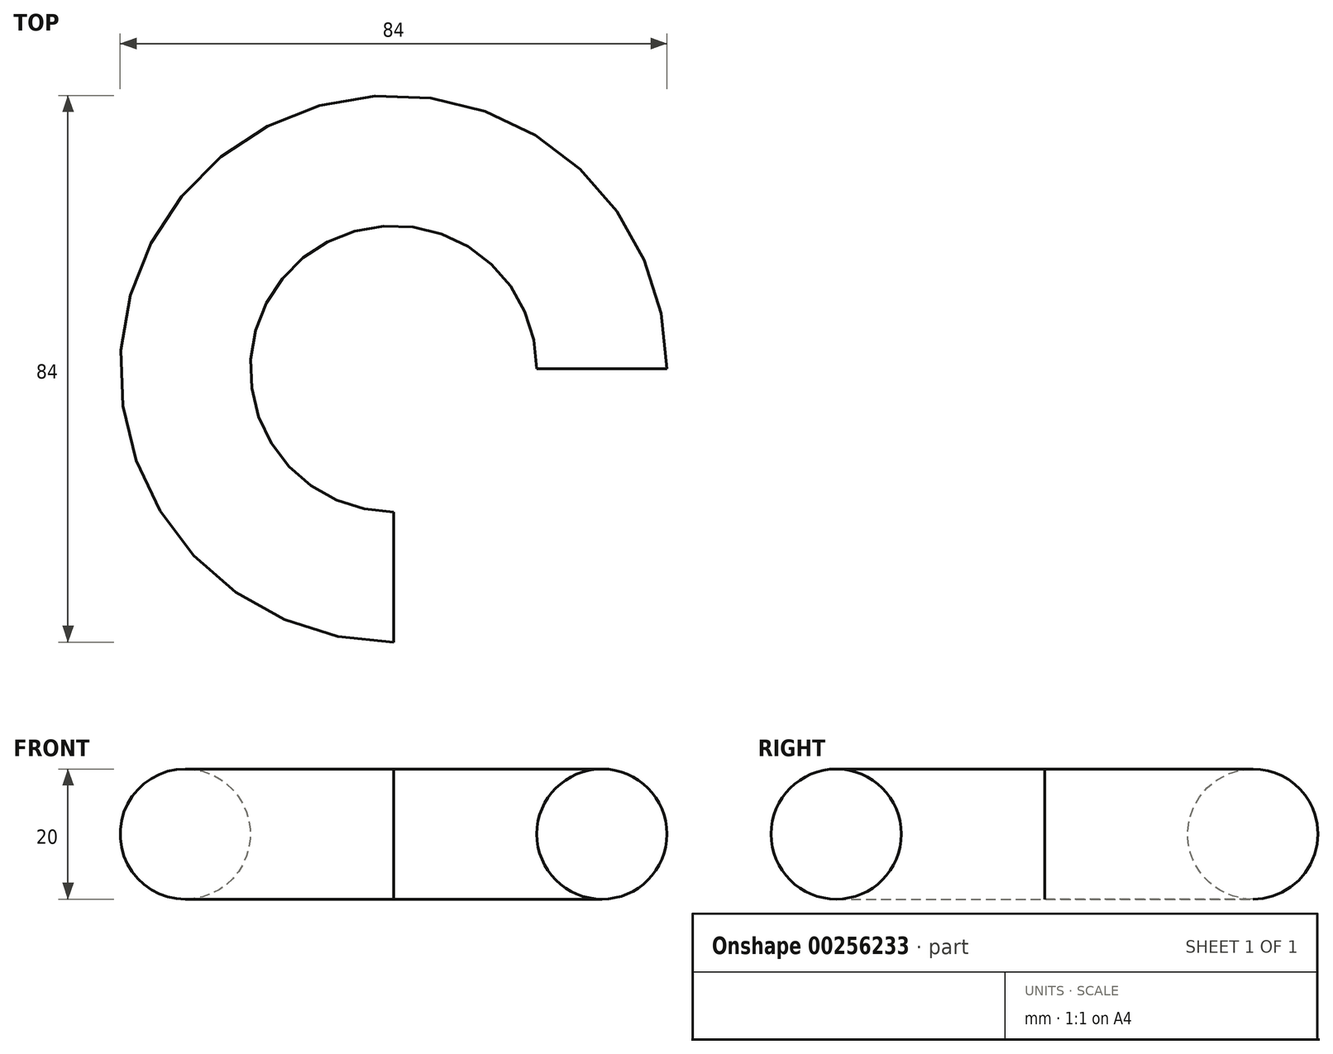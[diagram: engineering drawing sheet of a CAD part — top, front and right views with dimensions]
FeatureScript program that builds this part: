
annotation { "Feature Type Name" : "Feature", "Feature Type Description" : "" }
export const myFeature = defineFeature(function(context is Context, id is Id, definition is map)
    precondition{}
    {
        {
            var Q0;
            Q0=qCreatedBy(makeId("Front.planeOp"),FACE);
            var sketch = newSketch(context, id + "F0", { "sketchPlane" : qUnion([Q0])});
            skCircle(sketch, "E0", {"center": v(32, 0) * mm, "radius": 10 * mm});
            skLineSegment(sketch, "E1", {"start": v(0, 42.03) * mm, "end": v(0, -58.1) * mm, "construction": true});
            skSolve(sketch);
        }
        {
            var Q0;
            Q0=makeQuery(id+"F0.imprint","IMPRINT",FACE,{"disambiguationData":[TD([[makeQuery(id+"F0.imprint","IMPRINT",EDGE,{"derivedFrom":sQuery(id+"F0.wireOp",EDGE,"E0")}),1.0]])]});
            var Q1;
            Q1=sQuery(id+"F0.wireOp",EDGE,"E1");
            revolve(context, id + "F1", {"entities" : qUnion([Q0]), "axis" : qUnion([Q1]), "revolveType" : RevolveType.ONE_DIRECTION, "oppositeDirection" : true, "angle" : 270 * degree});
        }
    });
